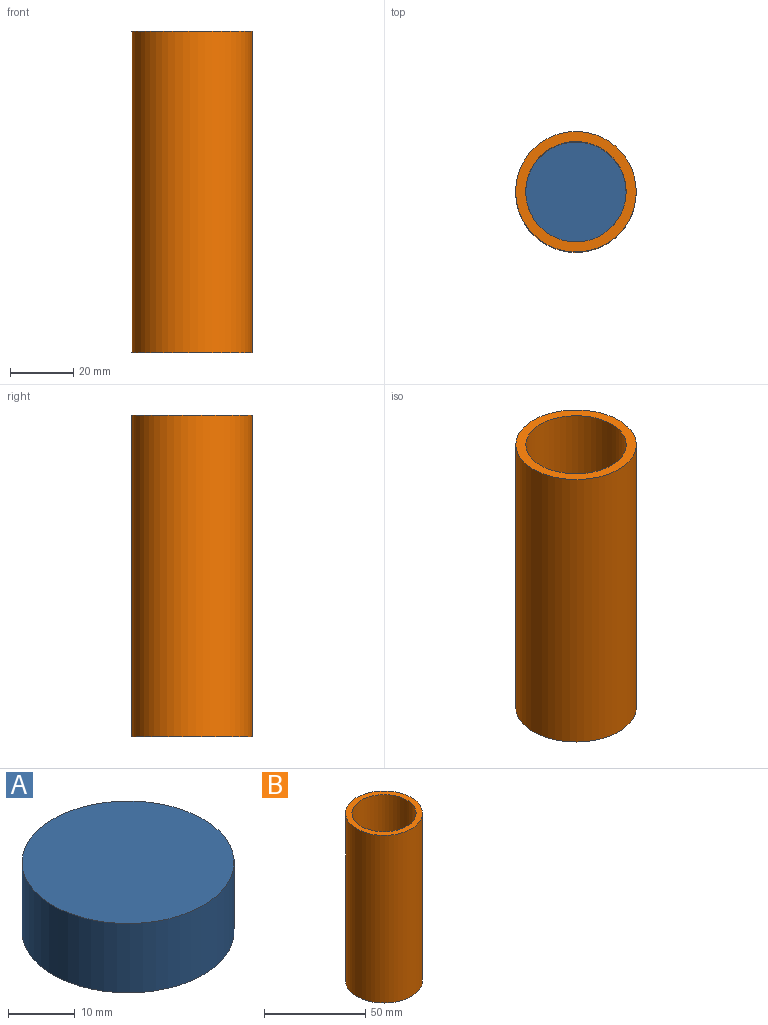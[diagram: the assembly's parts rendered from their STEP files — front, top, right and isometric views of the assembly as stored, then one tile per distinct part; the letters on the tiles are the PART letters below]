
ASSEMBLY  parts=2 mates=2
PART A: 3 faces, bbox 31.7x31.7x12.7 mm
  f0: cylinder r=15.86mm len=31.72mm, axis (0,0,-1), area 1265.8mm2, adj f1,f2
  f1: plane 31.72x31.72mm, normal (0,0,1), area 790.5mm2, adj f0
  f2: plane 31.72x31.72mm, normal (0,0,-1), area 790.5mm2, adj f0
PART B: 4 faces, bbox 38.1x38.1x101.6 mm
  f0: cylinder r=15.88mm len=101.6mm, axis (0,0,-1), area 10134.1mm2, adj f2,f3
  f1: cylinder r=19.05mm len=101.6mm, axis (0,0,-1), area 12161mm2, adj f2,f3
  f2: plane 38.1x38.1mm, normal (0,0,1), area 348.4mm2, adj f0,f1
  f3: plane 38.1x38.1mm, normal (0,0,-1), area 348.4mm2, adj f0,f1
PLACE A t=(-20.74,24.33,-5.27)mm
PLACE B t=(-20.74,24.33,-5.27)mm
MATE planar A.f0 <-> B.f0  axis (0,0,-1) through (-20.74,24.33,-5.27)mm
MATE cylindrical A.f0 <-> B.f0  axis (0,0,-1) through (-20.74,24.33,1.08)mm
